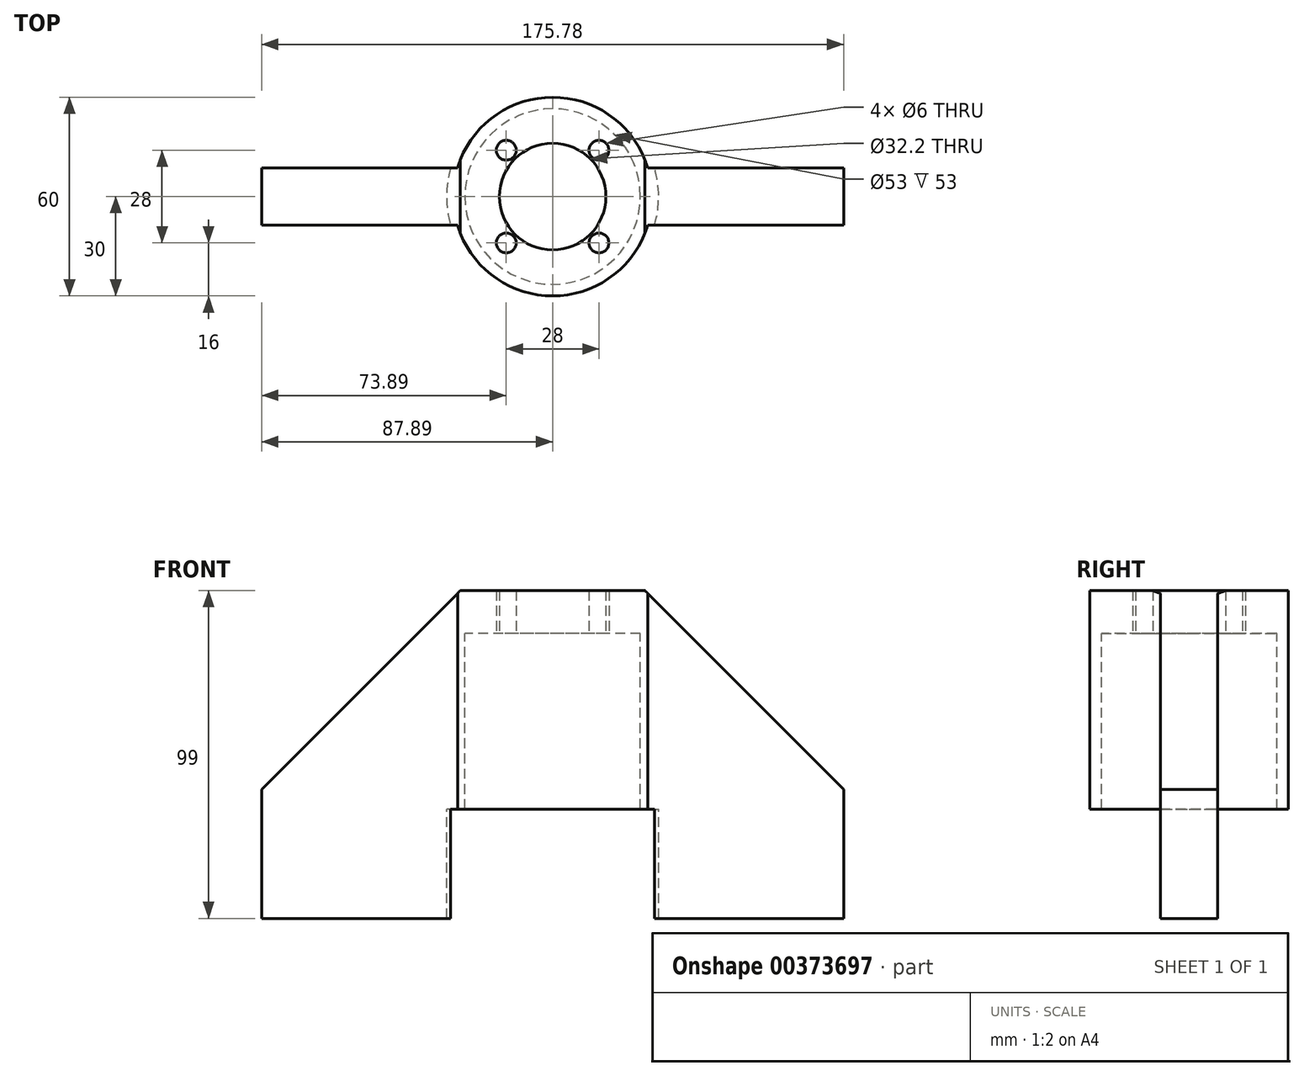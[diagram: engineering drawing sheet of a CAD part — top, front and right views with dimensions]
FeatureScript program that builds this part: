
annotation { "Feature Type Name" : "Feature", "Feature Type Description" : "" }
export const myFeature = defineFeature(function(context is Context, id is Id, definition is map)
    precondition{}
    {
        {
            var Q0;
            Q0=qCreatedBy(makeId("Top.planeOp"),FACE);
            var sketch = newSketch(context, id + "F0", { "sketchPlane" : qUnion([Q0])});
            skCircle(sketch, "E0", {"center": v(0, 0) * mm, "radius": 16.1 * mm});
            skCircle(sketch, "E1", {"center": v(0, 0) * mm, "radius": 26.5 * mm});
            skCircle(sketch, "E2", {"center": v(0, 0) * mm, "radius": 30 * mm});
            skCircle(sketch, "E3", {"center": v(14, 14) * mm, "radius": 3 * mm});
            skCircle(sketch, "E4", {"center": v(-14, 14) * mm, "radius": 3 * mm});
            skCircle(sketch, "E5", {"center": v(14, -14) * mm, "radius": 3 * mm});
            skCircle(sketch, "E6", {"center": v(-14, -14) * mm, "radius": 3 * mm});
            skLineSegment(sketch, "E7.bottom", {"start": v(-87.89, 8.65) * mm, "end": v(-28.73, 8.65) * mm});
            skLineSegment(sketch, "E7.top", {"start": v(-87.89, -8.65) * mm, "end": v(-28.73, -8.65) * mm});
            skLineSegment(sketch, "E7.left", {"start": v(-87.89, 8.65) * mm, "end": v(-87.89, -8.65) * mm});
            skLineSegment(sketch, "E7.right", {"start": v(87.89, 8.65) * mm, "end": v(87.89, -8.65) * mm});
            skLineSegment(sketch, "E8.trimOffspring", {"start": v(28.73, 8.65) * mm, "end": v(87.89, 8.65) * mm});
            skLineSegment(sketch, "E9.trimOffspring", {"start": v(28.73, -8.65) * mm, "end": v(87.89, -8.65) * mm});
            skSolve(sketch);
        }
        {
            var Q0;
            Q0=makeQuery(id+"F0.imprint","IMPRINT",FACE,{"disambiguationData":[TD([[makeQuery(id+"F0.imprint","IMPRINT",EDGE,{"derivedFrom":sQuery(id+"F0.wireOp",EDGE,"E0")}),-1.0]])]});
            var Q1;
            Q1=makeQuery(id+"F0.imprint","IMPRINT",FACE,{"disambiguationData":[TD([[makeQuery(id+"F0.imprint","IMPRINT",EDGE,{"derivedFrom":sQuery(id+"F0.wireOp",EDGE,"E1")}),-1.0]])]});
            var Q2;
            Q2=makeQuery(id+"F0.imprint","IMPRINT",FACE,{"disambiguationData":[TD([[makeQuery(id+"F0.imprint","IMPRINT",EDGE,{"derivedFrom":sQuery(id+"F0.wireOp",EDGE,"E7.right")}),-1.0]])]});
            var Q3;
            {var subQ0=sQuery(id+"F0.wireOp",EDGE,"E7.bottom");Q3=makeQuery(id+"F0.imprint","IMPRINT",FACE,{"disambiguationData":[TD([[makeQuery(id+"F0.imprint","IMPRINT",EDGE,{"derivedFrom":subQ0}),-1.0]])]});}
            extrude(context, id + "F1", {"entities" : qUnion([Q0, Q1, Q2, Q3]), "depth" : 13 * mm, "offsetDistance" : 25 * mm});
        }
        {
            var Q0;
            Q0=makeQuery(id+"F0.imprint","IMPRINT",FACE,{"disambiguationData":[TD([[makeQuery(id+"F0.imprint","IMPRINT",EDGE,{"derivedFrom":sQuery(id+"F0.wireOp",EDGE,"E1")}),-1.0]])]});
            var Q1;
            Q1=makeQuery(id+"F0.imprint","IMPRINT",FACE,{"disambiguationData":[TD([[makeQuery(id+"F0.imprint","IMPRINT",EDGE,{"derivedFrom":sQuery(id+"F0.wireOp",EDGE,"E7.right")}),-1.0]])]});
            var Q2;
            {var subQ0=sQuery(id+"F0.wireOp",EDGE,"E7.bottom");Q2=makeQuery(id+"F0.imprint","IMPRINT",FACE,{"disambiguationData":[TD([[makeQuery(id+"F0.imprint","IMPRINT",EDGE,{"derivedFrom":subQ0}),-1.0]])]});}
            extrude(context, id + "F2", {"entities" : qUnion([Q0, Q1, Q2]), "operationType" : NewBodyOperationType.ADD, "oppositeDirection" : true, "depth" : 53 * mm, "offsetDistance" : 25 * mm});
        }
        {
            var Q0;
            Q0=makeQuery(id+"F1.opExtrude","CAP_EDGE",EDGE,{"disambiguationData":[OSD([sQuery(id+"F0.wireOp",EDGE,"E7.right")])],"isStart":false});
            var Q1;
            Q1=makeQuery(id+"F1.opExtrude","CAP_EDGE",EDGE,{"disambiguationData":[OSD([sQuery(id+"F0.wireOp",EDGE,"E7.left")])],"isStart":false});
            chamfer(context, id + "F3", {"entities" : qUnion([Q0, Q1]), "width" : 60 * mm, "tangentPropagation" : true});
        }
        {
            var Q0;
            Q0=makeQuery(id+"F2.opExtrude","CAP_FACE",FACE,{"disambiguationData":[OSD([sQuery(id+"F0.wireOp",EDGE,"E1"),sQuery(id+"F0.wireOp",EDGE,"E2"),sQuery(id+"F0.wireOp",EDGE,"E7.bottom"),sQuery(id+"F0.wireOp",EDGE,"E7.top"),sQuery(id+"F0.wireOp",EDGE,"E7.left"),sQuery(id+"F0.wireOp",EDGE,"E7.right"),sQuery(id+"F0.wireOp",EDGE,"E8.trimOffspring"),sQuery(id+"F0.wireOp",EDGE,"E9.trimOffspring")])],"isStart":false});
            var sketch = newSketch(context, id + "F4", { "sketchPlane" : qUnion([Q0])});
            skCircle(sketch, "E10", {"center": v(0, 0) * mm, "radius": 32 * mm});
            skLineSegment(sketch, "E11.bottom", {"start": v(-87.89, -8.65) * mm, "end": v(-28.73, -8.65) * mm});
            skLineSegment(sketch, "E11.top", {"start": v(-87.89, 8.65) * mm, "end": v(-28.73, 8.65) * mm});
            skLineSegment(sketch, "E11.left", {"start": v(-87.89, -8.65) * mm, "end": v(-87.89, 8.65) * mm});
            skLineSegment(sketch, "E11.right", {"start": v(-28.73, -8.65) * mm, "end": v(-28.73, 8.65) * mm});
            skLineSegment(sketch, "E12.bottom", {"start": v(87.89, -8.65) * mm, "end": v(28.73, -8.65) * mm});
            skLineSegment(sketch, "E12.top", {"start": v(87.89, 8.65) * mm, "end": v(28.73, 8.65) * mm});
            skLineSegment(sketch, "E12.left", {"start": v(87.89, -8.65) * mm, "end": v(87.89, 8.65) * mm});
            skLineSegment(sketch, "E12.right", {"start": v(28.73, -8.65) * mm, "end": v(28.73, 8.65) * mm});
            skSolve(sketch);
        }
        {
            var Q0;
            {var subQ5=sQuery(id+"F4.wireOp",EDGE,"E11.left");Q0=makeQuery(id+"F4.imprint","IMPRINT",FACE,{"disambiguationData":[TD([[makeQuery(id+"F4.imprint","IMPRINT",EDGE,{"derivedFrom":subQ5}),-1.0]])]});}
            var Q1;
            {var subQ5=sQuery(id+"F4.wireOp",EDGE,"E12.left");Q1=makeQuery(id+"F4.imprint","IMPRINT",FACE,{"disambiguationData":[TD([[makeQuery(id+"F4.imprint","IMPRINT",EDGE,{"derivedFrom":subQ5}),1.0]])]});}
            extrude(context, id + "F5", {"entities" : qUnion([Q0, Q1]), "operationType" : NewBodyOperationType.ADD, "depth" : 33 * mm, "offsetDistance" : 25 * mm});
        }
    });
